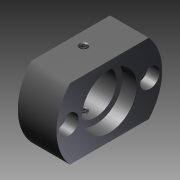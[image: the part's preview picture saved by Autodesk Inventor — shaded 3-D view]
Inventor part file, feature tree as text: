
AUTODESK INVENTOR PART (.ipt)
format: ipt  version: 2016 (Build 200138000, 138)  size: 170,496 bytes
history: native  units: mm
features: other x21, sketch x5, revolve x4, thread x3, extrude x1, pattern_linear x1
ambient origin geometry x8: Origin, YZ Plane, XZ Plane, XY Plane, X Axis, Y Axis, Z Axis, Center Point
bodies: Solid1 (feature_tree)
feature tree (35):
  revolve  "Revolution1"  [1 undecoded]
  extrude  "Extrusion1"  Depth=14.147mm TaperAngle=0.0deg
  revolve  "Revolution2"  Angle=360.0deg
  thread  "Thread1"  [1 undecoded]
  pattern_linear  "Rectangular Pattern1"  Spacing1=0.0mm  [1 undecoded]
  revolve  "Revolution3"  [1 undecoded]
  thread  "Thread2"  [1 undecoded]
  revolve  "Revolution4"  [1 undecoded]
  thread  "Thread3"  [1 undecoded]
  other  "to_bearings_XY"
  other  "to_bearings_YZ"
  other  "to_bearings_ZX"
  other  "to_bearings_X"
  other  "to_bearings_Y"
  other  "to_bearings_Z"
  other  "to_bearings_Center"
  other  "to_screw1_XY"
  other  "to_screw1_YZ"
  other  "to_screw1_ZX"
  other  "to_screw1_X"
  other  "to_screw1_Y"
  other  "to_screw1_Z"
  other  "to_screw1_Center"
  other  "to_screw2_XY"
  other  "to_screw2_YZ"
  other  "to_screw2_ZX"
  other  "to_screw2_X"
  other  "to_screw2_Y"
  other  "to_screw2_Z"
  other  "to_screw2_Center"
  sketch  "Sketch_1"  dims[d0=360.0deg d1=24.0mm d2=0.0mm]
  sketch  "Sketch_2"  dims[d3=360.0deg d4=14.147mm d5=0.0mm]
  sketch  "Sketch_3"  dims[d6=20.0mm d8=46.0mm d9=10.0mm d11=0.0mm d12=360.0deg d13=7.484mm d14=0.0mm]
  sketch  "Sketch_4"  dims[d15=360.0deg]
  sketch  "Sketch_6"  dims[d16=7.484mm d17=0.0mm d18=0.0mm]
note: 7 required parameter values undecoded (feature->parameter linkage not recoverable at this tier; creation-order binding heuristic only, values carry confidence <= 0.55)